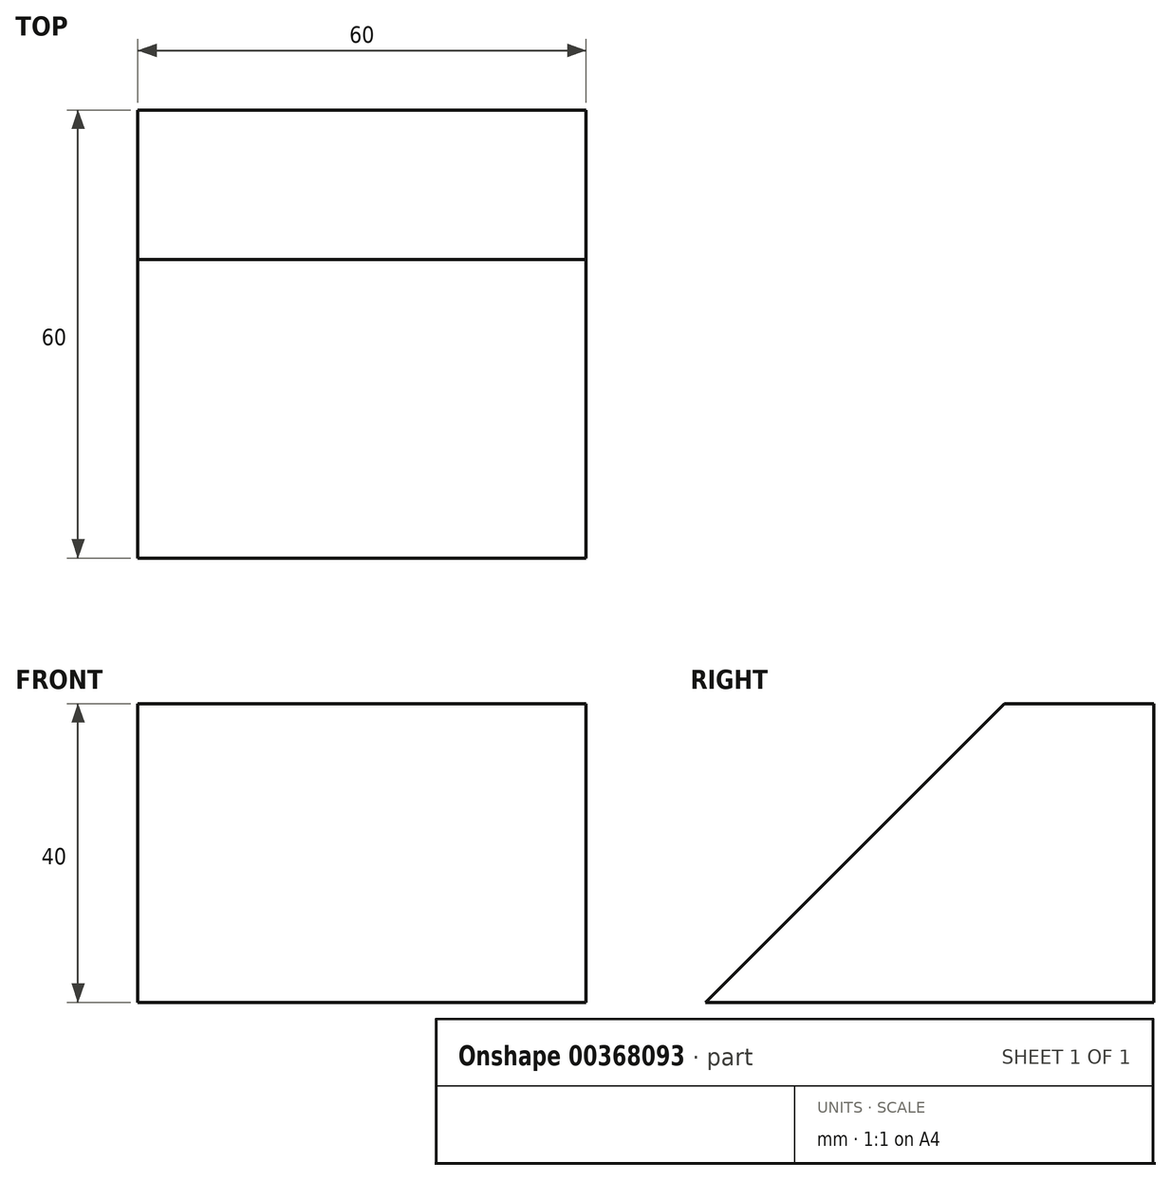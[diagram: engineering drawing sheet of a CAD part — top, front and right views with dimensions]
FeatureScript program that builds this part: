
annotation { "Feature Type Name" : "Feature", "Feature Type Description" : "" }
export const myFeature = defineFeature(function(context is Context, id is Id, definition is map)
    precondition{}
    {
        {
            var Q0;
            Q0=qCreatedBy(makeId("Right.planeOp"),FACE);
            var sketch = newSketch(context, id + "F0", { "sketchPlane" : qUnion([Q0])});
            skLineSegment(sketch, "E0", {"start": v(0, 0) * mm, "end": v(-60, 0) * mm});
            skLineSegment(sketch, "E1", {"start": v(-60, 0) * mm, "end": v(-20, 40) * mm});
            skLineSegment(sketch, "E2", {"start": v(-20, 40) * mm, "end": v(0, 40) * mm});
            skLineSegment(sketch, "E3", {"start": v(0, 40) * mm, "end": v(0, 0) * mm});
            skPoint(sketch, "E4", {"position": v(-40, 30) * mm});
            skSolve(sketch);
        }
        {
            var Q0;
            Q0=makeQuery(id+"F0.imprint","IMPRINT",FACE,{"disambiguationData":[TD([[makeQuery(id+"F0.imprint","IMPRINT",EDGE,{"derivedFrom":sQuery(id+"F0.wireOp",EDGE,"E0")}),-1.0]])]});
            extrude(context, id + "F1", {"entities" : qUnion([Q0]), "endBound" : BoundingType.SYMMETRIC, "depth" : 60 * mm});
        }
    });
